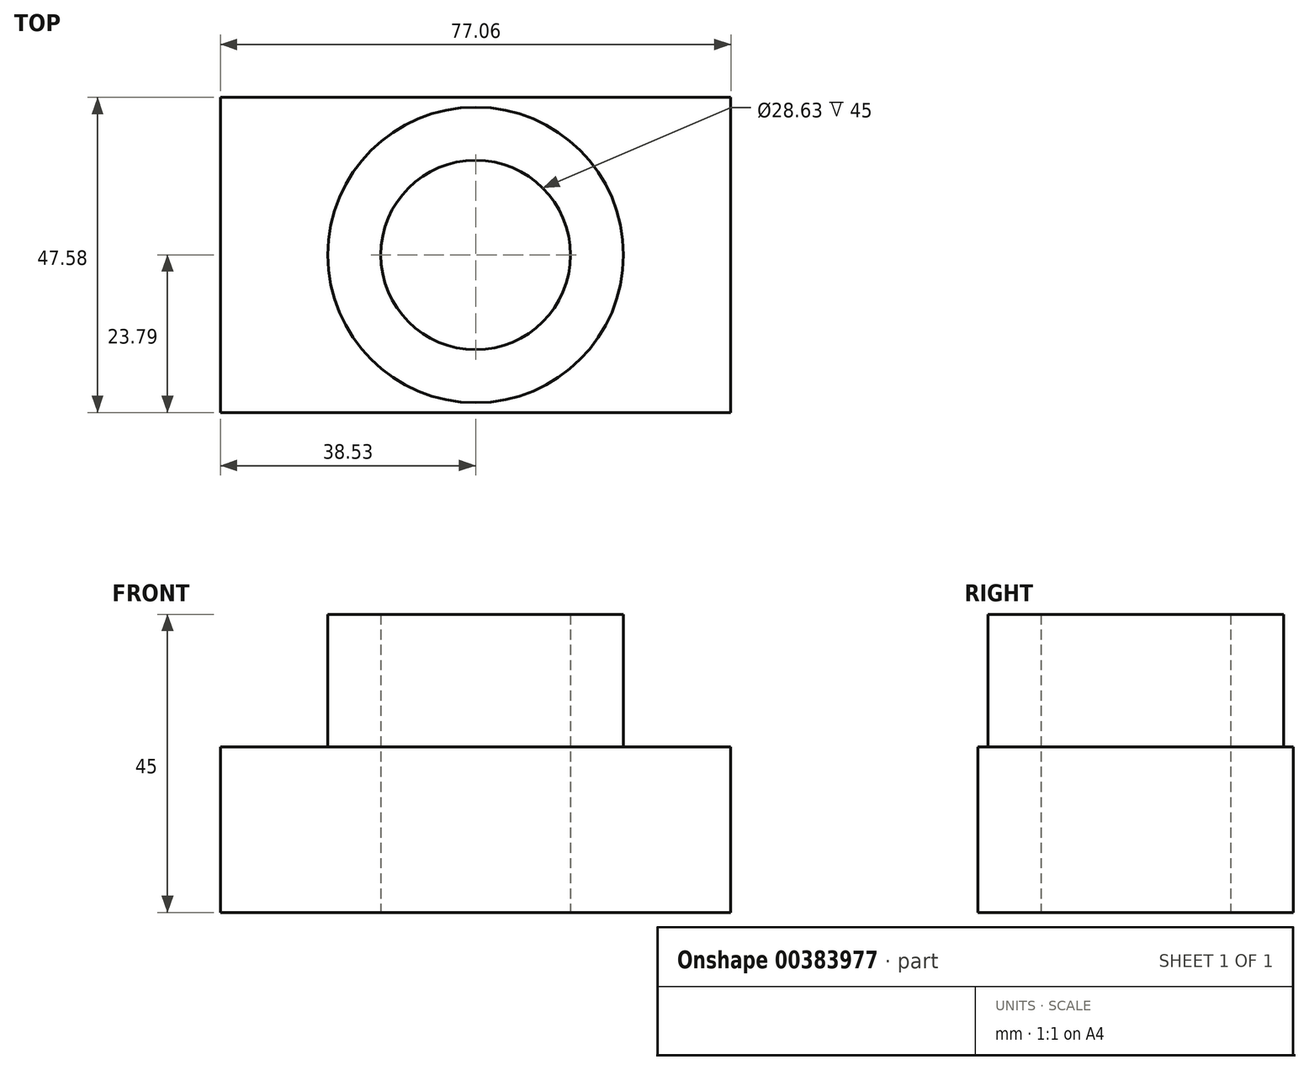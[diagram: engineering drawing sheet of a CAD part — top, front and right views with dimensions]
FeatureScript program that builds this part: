
annotation { "Feature Type Name" : "Feature", "Feature Type Description" : "" }
export const myFeature = defineFeature(function(context is Context, id is Id, definition is map)
    precondition{}
    {
        {
            var Q0;
            Q0=qCreatedBy(makeId("Top.planeOp"),FACE);
            var sketch = newSketch(context, id + "F0", { "sketchPlane" : qUnion([Q0])});
            skLineSegment(sketch, "E0.bottom", {"start": v(-38.53, -23.8) * mm, "end": v(38.53, -23.8) * mm});
            skLineSegment(sketch, "E0.top", {"start": v(-38.53, 23.8) * mm, "end": v(38.53, 23.8) * mm});
            skLineSegment(sketch, "E0.left", {"start": v(-38.53, -23.8) * mm, "end": v(-38.53, 23.8) * mm});
            skLineSegment(sketch, "E0.right", {"start": v(38.53, -23.8) * mm, "end": v(38.53, 23.8) * mm});
            skPoint(sketch, "E0.middle", {"position": v(0, 0) * mm});
            skCircle(sketch, "E1", {"center": v(0, 0) * mm, "radius": 14.32 * mm});
            skSolve(sketch);
        }
        {
            var Q0;
            Q0 = qSketchRegion(id + "F0", true);
            extrude(context, id + "F1", {"entities" : qUnion([Q0]), "depth" : 25 * mm});
        }
        {
            var Q0;
            Q0=qCreatedBy(makeId("Top.planeOp"),FACE);
            var sketch = newSketch(context, id + "F2", { "sketchPlane" : qUnion([Q0])});
            skCircle(sketch, "E2.0", {"center": v(0, 0) * mm, "radius": 14.32 * mm});
            skCircle(sketch, "E3.0", {"center": v(0, 0) * mm, "radius": 22.32 * mm});
            skSolve(sketch);
        }
        {
            var Q0;
            Q0 = qSketchRegion(id + "F2", true);
            extrude(context, id + "F3", {"entities" : qUnion([Q0]), "operationType" : NewBodyOperationType.ADD, "depth" : 45 * mm});
        }
    });
